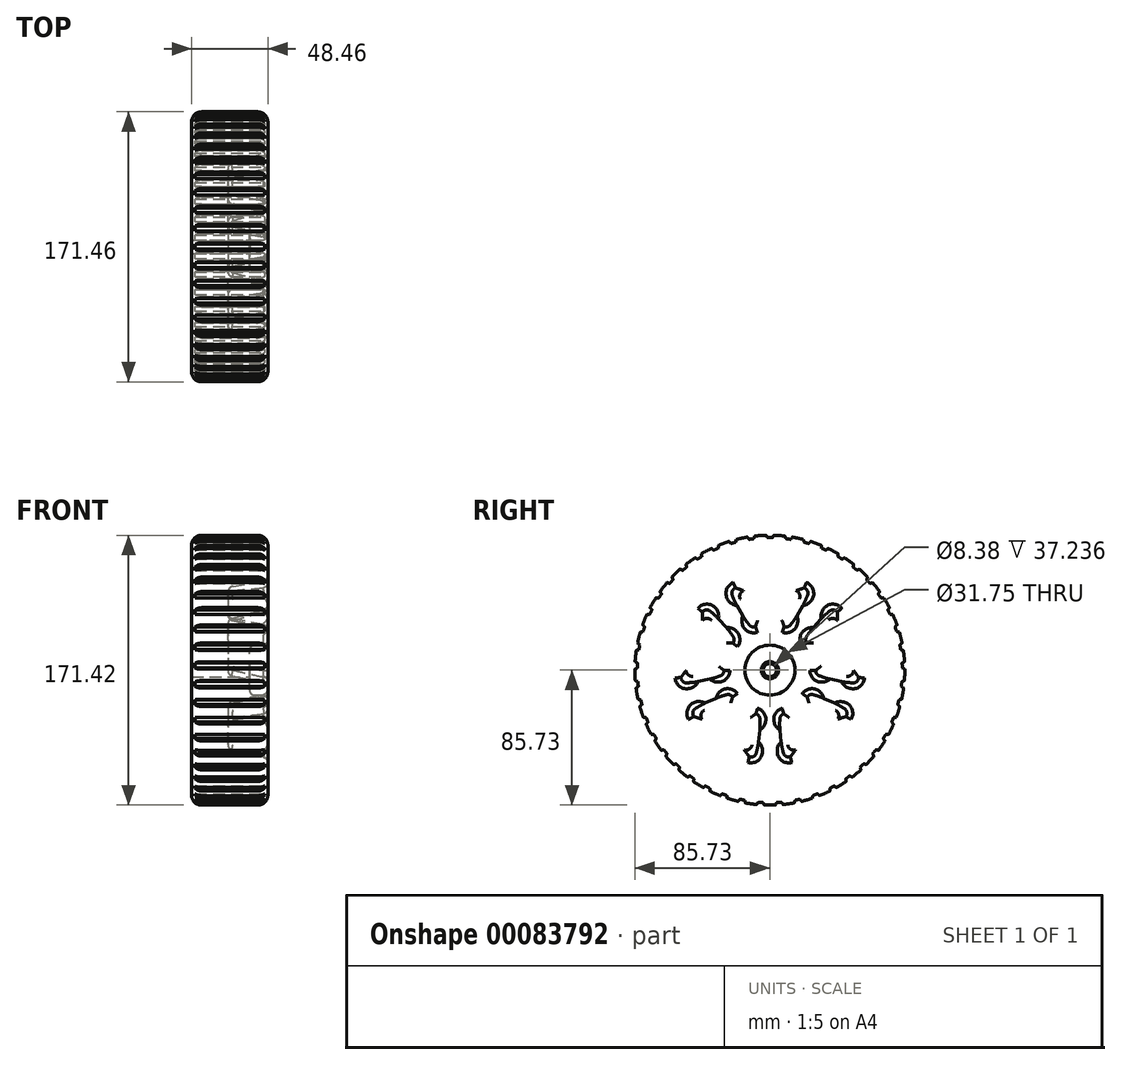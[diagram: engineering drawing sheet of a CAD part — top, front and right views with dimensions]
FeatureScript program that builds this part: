
annotation { "Feature Type Name" : "Feature", "Feature Type Description" : "" }
export const myFeature = defineFeature(function(context is Context, id is Id, definition is map)
    precondition{}
    {
        {
            var Q0;
            Q0=qCreatedBy(makeId("Front.planeOp"),FACE);
            var sketch = newSketch(context, id + "F0", { "sketchPlane" : qUnion([Q0])});
            skLineSegment(sketch, "E0", {"start": v(0, 85.73) * mm, "end": v(17.78, 85.73) * mm});
            skLineSegment(sketch, "E1", {"start": v(24.13, 79.38) * mm, "end": v(24.13, 19.05) * mm});
            skLineSegment(sketch, "E2", {"start": v(20.96, 15.88) * mm, "end": v(15.67, 15.88) * mm});
            skLineSegment(sketch, "E3", {"start": v(12.5, 12.7) * mm, "end": v(12.5, 5.46) * mm});
            skLineSegment(sketch, "E4", {"start": v(27.52, 0) * mm, "end": v(-27.22, 0) * mm});
            skLineSegment(sketch, "E5", {"start": v(0, 85.73) * mm, "end": v(-17.98, 85.73) * mm});
            skLineSegment(sketch, "E6", {"start": v(-24.33, 79.38) * mm, "end": v(-24.33, 4.2) * mm});
            skLineSegment(sketch, "E7", {"start": v(-24.33, 4.2) * mm, "end": v(12.9, 4.2) * mm});
            skPoint(sketch, "E8.end.orphan", {"position": v(0, 7.03) * mm});
            skLineSegment(sketch, "E9", {"start": v(12.5, 5.46) * mm, "end": v(12.9, 5.46) * mm});
            skLineSegment(sketch, "E10", {"start": v(12.9, 5.46) * mm, "end": v(12.9, 4.2) * mm});
            skPoint(sketch, "E11.visualSharp", {"position": v(-24.33, 85.73) * mm});
            skArc(sketch, "E11.filletArc", {"start": v(-17.98, 85.73) * mm, "mid": v(-22.47, 83.87) * mm, "end": v(-24.33, 79.38) * mm});
            skPoint(sketch, "E12.visualSharp", {"position": v(24.13, 85.73) * mm});
            skArc(sketch, "E12.filletArc", {"start": v(24.13, 79.38) * mm, "mid": v(22.27, 83.87) * mm, "end": v(17.78, 85.73) * mm});
            skPoint(sketch, "E13.visualSharp", {"position": v(24.13, 15.88) * mm});
            skArc(sketch, "E13.filletArc", {"start": v(20.96, 15.88) * mm, "mid": v(23.2, 16.8) * mm, "end": v(24.13, 19.05) * mm});
            skPoint(sketch, "E14.visualSharp", {"position": v(12.5, 15.88) * mm});
            skArc(sketch, "E14.filletArc", {"start": v(15.67, 15.88) * mm, "mid": v(13.43, 14.95) * mm, "end": v(12.5, 12.7) * mm});
            skSolve(sketch);
        }
        {
            var Q0;
            Q0=makeQuery(id+"F0.imprint","IMPRINT",FACE,{"disambiguationData":[TD([[makeQuery(id+"F0.imprint","IMPRINT",EDGE,{"derivedFrom":sQuery(id+"F0.wireOp",EDGE,"E0")}),-1.0]])]});
            var Q1;
            Q1=sQuery(id+"F0.wireOp",EDGE,"E4");
            revolve(context, id + "F1", {"entities" : qUnion([Q0]), "axis" : qUnion([Q1]), "revolveType" : RevolveType.FULL});
        }
        {
            var Q0;
            Q0=makeQuery(id+"F1.opRevolve","SWEPT_FACE",FACE,{"disambiguationData":[OSD([sQuery(id+"F0.wireOp",EDGE,"E1")])]});
            var sketch = newSketch(context, id + "F2", { "sketchPlane" : qUnion([Q0])});
            skArc(sketch, "E15", {"start": v(12.14, 25.87) * mm, "mid": v(0, 28.58) * mm, "end": v(-12.14, 25.87) * mm});
            skArc(sketch, "E16", {"start": v(26.46, 50.66) * mm, "mid": v(0, 57.15) * mm, "end": v(-26.46, 50.66) * mm});
            skLineSegment(sketch, "E17", {"start": v(-12.14, 25.87) * mm, "end": v(-26.46, 50.66) * mm});
            skLineSegment(sketch, "E18", {"start": v(12.14, 25.87) * mm, "end": v(26.46, 50.66) * mm});
            skPoint(sketch, "E19.visualSharp", {"position": v(-26.46, 50.66) * mm});
            skPoint(sketch, "E20.visualSharp", {"position": v(26.46, 50.66) * mm});
            skPoint(sketch, "E21.visualSharp", {"position": v(12.14, 25.87) * mm});
            skPoint(sketch, "E22.visualSharp", {"position": v(-12.14, 25.87) * mm});
            skLineSegment(sketch, "E23.1.0", {"start": v(-28.35, -3.56) * mm, "end": v(-56.35, -9.5) * mm});
            skArc(sketch, "E23.1.1", {"start": v(-40, 40.82) * mm, "mid": v(-54.35, 17.66) * mm, "end": v(-56.35, -9.5) * mm});
            skLineSegment(sketch, "E23.1.2", {"start": v(-20.85, 19.54) * mm, "end": v(-40, 40.82) * mm});
            skArc(sketch, "E23.1.3", {"start": v(-20.85, 19.54) * mm, "mid": v(-27.18, 8.83) * mm, "end": v(-28.35, -3.56) * mm});
            skLineSegment(sketch, "E23.2.0", {"start": v(-5.38, -28.06) * mm, "end": v(-8.37, -56.53) * mm});
            skArc(sketch, "E23.2.1", {"start": v(-51.18, -25.43) * mm, "mid": v(-33.6, -46.24) * mm, "end": v(-8.37, -56.53) * mm});
            skLineSegment(sketch, "E23.2.2", {"start": v(-25.03, -13.79) * mm, "end": v(-51.18, -25.43) * mm});
            skArc(sketch, "E23.2.3", {"start": v(-25.03, -13.79) * mm, "mid": v(-16.8, -23.12) * mm, "end": v(-5.38, -28.06) * mm});
            skLineSegment(sketch, "E23.3.0", {"start": v(25.03, -13.79) * mm, "end": v(51.18, -25.43) * mm});
            skArc(sketch, "E23.3.1", {"start": v(8.37, -56.53) * mm, "mid": v(33.6, -46.24) * mm, "end": v(51.18, -25.43) * mm});
            skLineSegment(sketch, "E23.3.2", {"start": v(5.38, -28.06) * mm, "end": v(8.37, -56.53) * mm});
            skArc(sketch, "E23.3.3", {"start": v(5.38, -28.06) * mm, "mid": v(16.8, -23.12) * mm, "end": v(25.03, -13.79) * mm});
            skLineSegment(sketch, "E23.4.0", {"start": v(20.85, 19.54) * mm, "end": v(40, 40.82) * mm});
            skArc(sketch, "E23.4.1", {"start": v(56.35, -9.5) * mm, "mid": v(54.35, 17.66) * mm, "end": v(40, 40.82) * mm});
            skLineSegment(sketch, "E23.4.2", {"start": v(28.35, -3.56) * mm, "end": v(56.35, -9.5) * mm});
            skArc(sketch, "E23.4.3", {"start": v(28.35, -3.56) * mm, "mid": v(27.18, 8.83) * mm, "end": v(20.85, 19.54) * mm});
            skSolve(sketch);
        }
        {
            var Q0;
            Q0 = qSketchRegion(id + "F2", true);
            extrude(context, id + "F3", {"entities" : qUnion([Q0]), "operationType" : NewBodyOperationType.REMOVE, "oppositeDirection" : true, "depth" : 25.4 * mm, "hasDraft" : true, "draftAngle" : 10 * degree, "draftPullDirection" : true});
        }
        {
            var Q0;
            Q0=makeQuery(id+"F3.boolean.opBoolean","COPY",FACE,{"derivedFrom":makeQuery(id+"F3.opExtrude","SWEPT_FACE",FACE,{"disambiguationData":[OSD([sQuery(id+"F2.wireOp",EDGE,"E16")])]})});
            var Q1;
            Q1=makeQuery(id+"F3.boolean.opBoolean","COPY",FACE,{"derivedFrom":makeQuery(id+"F3.opExtrude","SWEPT_FACE",FACE,{"disambiguationData":[OSD([sQuery(id+"F2.wireOp",EDGE,"E15")])]})});
            var Q2;
            Q2=makeQuery(id+"F3.boolean.opBoolean","COPY",FACE,{"derivedFrom":makeQuery(id+"F3.opExtrude","CAP_FACE",FACE,{"disambiguationData":[OSD([sQuery(id+"F2.wireOp",EDGE,"E15"),sQuery(id+"F2.wireOp",EDGE,"E16"),sQuery(id+"F2.wireOp",EDGE,"E17"),sQuery(id+"F2.wireOp",EDGE,"E18")])],"isStart":false})});
            var Q3;
            Q3=makeQuery(id+"F3.boolean.opBoolean","COPY",FACE,{"derivedFrom":makeQuery(id+"F3.opExtrude","CAP_FACE",FACE,{"disambiguationData":[OSD([sQuery(id+"F2.wireOp",EDGE,"E23.1.0"),sQuery(id+"F2.wireOp",EDGE,"E23.1.1"),sQuery(id+"F2.wireOp",EDGE,"E23.1.2"),sQuery(id+"F2.wireOp",EDGE,"E23.1.3")])],"isStart":false})});
            var Q4;
            Q4=makeQuery(id+"F3.boolean.opBoolean","COPY",FACE,{"derivedFrom":makeQuery(id+"F3.opExtrude","SWEPT_FACE",FACE,{"disambiguationData":[OSD([sQuery(id+"F2.wireOp",EDGE,"E23.1.1")])]})});
            var Q5;
            Q5=makeQuery(id+"F3.boolean.opBoolean","COPY",FACE,{"derivedFrom":makeQuery(id+"F3.opExtrude","SWEPT_FACE",FACE,{"disambiguationData":[OSD([sQuery(id+"F2.wireOp",EDGE,"E23.1.3")])]})});
            var Q6;
            Q6=makeQuery(id+"F3.boolean.opBoolean","COPY",FACE,{"derivedFrom":makeQuery(id+"F3.opExtrude","CAP_FACE",FACE,{"disambiguationData":[OSD([sQuery(id+"F2.wireOp",EDGE,"E23.3.0"),sQuery(id+"F2.wireOp",EDGE,"E23.3.1"),sQuery(id+"F2.wireOp",EDGE,"E23.3.2"),sQuery(id+"F2.wireOp",EDGE,"E23.3.3")])],"isStart":false})});
            var Q7;
            Q7=makeQuery(id+"F3.boolean.opBoolean","COPY",FACE,{"derivedFrom":makeQuery(id+"F3.opExtrude","CAP_FACE",FACE,{"disambiguationData":[OSD([sQuery(id+"F2.wireOp",EDGE,"E23.2.0"),sQuery(id+"F2.wireOp",EDGE,"E23.2.1"),sQuery(id+"F2.wireOp",EDGE,"E23.2.2"),sQuery(id+"F2.wireOp",EDGE,"E23.2.3")])],"isStart":false})});
            var Q8;
            Q8=makeQuery(id+"F3.boolean.opBoolean","COPY",FACE,{"derivedFrom":makeQuery(id+"F3.opExtrude","SWEPT_FACE",FACE,{"disambiguationData":[OSD([sQuery(id+"F2.wireOp",EDGE,"E23.2.3")])]})});
            var Q9;
            Q9=makeQuery(id+"F3.boolean.opBoolean","COPY",FACE,{"derivedFrom":makeQuery(id+"F3.opExtrude","SWEPT_FACE",FACE,{"disambiguationData":[OSD([sQuery(id+"F2.wireOp",EDGE,"E23.3.3")])]})});
            var Q10;
            Q10=makeQuery(id+"F3.boolean.opBoolean","COPY",FACE,{"derivedFrom":makeQuery(id+"F3.opExtrude","SWEPT_FACE",FACE,{"disambiguationData":[OSD([sQuery(id+"F2.wireOp",EDGE,"E23.4.3")])]})});
            var Q11;
            Q11=makeQuery(id+"F3.boolean.opBoolean","COPY",FACE,{"derivedFrom":makeQuery(id+"F3.opExtrude","CAP_FACE",FACE,{"disambiguationData":[OSD([sQuery(id+"F2.wireOp",EDGE,"E23.4.0"),sQuery(id+"F2.wireOp",EDGE,"E23.4.1"),sQuery(id+"F2.wireOp",EDGE,"E23.4.2"),sQuery(id+"F2.wireOp",EDGE,"E23.4.3")])],"isStart":false})});
            var Q12;
            Q12=makeQuery(id+"F3.boolean.opBoolean","COPY",FACE,{"derivedFrom":makeQuery(id+"F3.opExtrude","SWEPT_FACE",FACE,{"disambiguationData":[OSD([sQuery(id+"F2.wireOp",EDGE,"E23.4.1")])]})});
            var Q13;
            Q13=makeQuery(id+"F3.boolean.opBoolean","COPY",FACE,{"derivedFrom":makeQuery(id+"F3.opExtrude","SWEPT_FACE",FACE,{"disambiguationData":[OSD([sQuery(id+"F2.wireOp",EDGE,"E23.3.1")])]})});
            var Q14;
            Q14=makeQuery(id+"F3.boolean.opBoolean","COPY",FACE,{"derivedFrom":makeQuery(id+"F3.opExtrude","SWEPT_FACE",FACE,{"disambiguationData":[OSD([sQuery(id+"F2.wireOp",EDGE,"E23.2.1")])]})});
            fillet(context, id + "F4", {"entities" : qUnion([Q0, Q1, Q2, Q3, Q4, Q5, Q6, Q7, Q8, Q9, Q10, Q11, Q12, Q13, Q14]), "radius" : 3.8 * mm, "tangentPropagation" : true, "allowEdgeOverflow" : false});
        }
        {
            var Q0;
            Q0=qCreatedBy(makeId("Right.planeOp"),FACE);
            var sketch = newSketch(context, id + "F5", { "sketchPlane" : qUnion([Q0])});
            skLineSegment(sketch, "E24", {"start": v(-1.59, 84.14) * mm, "end": v(1.59, 84.14) * mm});
            skLineSegment(sketch, "E25", {"start": v(-1.59, 84.14) * mm, "end": v(-3.18, 87.34) * mm});
            skLineSegment(sketch, "E26", {"start": v(1.59, 84.14) * mm, "end": v(3.17, 87.34) * mm});
            skLineSegment(sketch, "E27", {"start": v(-3.18, 87.34) * mm, "end": v(3.18, 87.34) * mm});
            skLineSegment(sketch, "E28.1.0", {"start": v(-15.3, 86.05) * mm, "end": v(-9.01, 86.94) * mm});
            skLineSegment(sketch, "E28.1.1", {"start": v(-13.28, 83.1) * mm, "end": v(-10.14, 83.54) * mm});
            skLineSegment(sketch, "E28.1.2", {"start": v(-10.14, 83.54) * mm, "end": v(-9.01, 86.94) * mm});
            skLineSegment(sketch, "E28.1.3", {"start": v(-13.28, 83.1) * mm, "end": v(-15.3, 86.05) * mm});
            skLineSegment(sketch, "E28.2.0", {"start": v(-27.13, 83.09) * mm, "end": v(-21.02, 84.84) * mm});
            skLineSegment(sketch, "E28.2.1", {"start": v(-24.72, 80.44) * mm, "end": v(-21.67, 81.32) * mm});
            skLineSegment(sketch, "E28.2.2", {"start": v(-21.67, 81.32) * mm, "end": v(-21.02, 84.84) * mm});
            skLineSegment(sketch, "E28.2.3", {"start": v(-24.72, 80.44) * mm, "end": v(-27.13, 83.09) * mm});
            skLineSegment(sketch, "E28.3.0", {"start": v(-38.43, 78.5) * mm, "end": v(-32.63, 81.08) * mm});
            skLineSegment(sketch, "E28.3.1", {"start": v(-35.67, 76.22) * mm, "end": v(-32.77, 77.5) * mm});
            skLineSegment(sketch, "E28.3.2", {"start": v(-32.77, 77.5) * mm, "end": v(-32.63, 81.08) * mm});
            skLineSegment(sketch, "E28.3.3", {"start": v(-35.67, 76.22) * mm, "end": v(-38.43, 78.5) * mm});
            skLineSegment(sketch, "E28.4.0", {"start": v(-48.98, 72.4) * mm, "end": v(-43.6, 75.76) * mm});
            skLineSegment(sketch, "E28.4.1", {"start": v(-45.93, 70.51) * mm, "end": v(-43.24, 72.2) * mm});
            skLineSegment(sketch, "E28.4.2", {"start": v(-43.24, 72.2) * mm, "end": v(-43.6, 75.76) * mm});
            skLineSegment(sketch, "E28.4.3", {"start": v(-45.93, 70.51) * mm, "end": v(-48.98, 72.4) * mm});
            skLineSegment(sketch, "E28.5.0", {"start": v(-58.58, 64.87) * mm, "end": v(-53.71, 68.95) * mm});
            skLineSegment(sketch, "E28.5.1", {"start": v(-55.3, 63.43) * mm, "end": v(-52.87, 65.47) * mm});
            skLineSegment(sketch, "E28.5.2", {"start": v(-52.87, 65.47) * mm, "end": v(-53.71, 68.95) * mm});
            skLineSegment(sketch, "E28.5.3", {"start": v(-55.3, 63.43) * mm, "end": v(-58.58, 64.87) * mm});
            skLineSegment(sketch, "E28.6.0", {"start": v(-67.03, 56.09) * mm, "end": v(-62.79, 60.8) * mm});
            skLineSegment(sketch, "E28.6.1", {"start": v(-63.59, 55.12) * mm, "end": v(-61.46, 57.48) * mm});
            skLineSegment(sketch, "E28.6.2", {"start": v(-61.46, 57.48) * mm, "end": v(-62.79, 60.8) * mm});
            skLineSegment(sketch, "E28.6.3", {"start": v(-63.59, 55.12) * mm, "end": v(-67.03, 56.09) * mm});
            skLineSegment(sketch, "E28.7.0", {"start": v(-74.19, 46.21) * mm, "end": v(-70.64, 51.47) * mm});
            skLineSegment(sketch, "E28.7.1", {"start": v(-70.64, 45.73) * mm, "end": v(-68.87, 48.37) * mm});
            skLineSegment(sketch, "E28.7.2", {"start": v(-68.87, 48.37) * mm, "end": v(-70.64, 51.47) * mm});
            skLineSegment(sketch, "E28.7.3", {"start": v(-70.64, 45.73) * mm, "end": v(-74.19, 46.21) * mm});
            skLineSegment(sketch, "E28.8.0", {"start": v(-79.9, 35.44) * mm, "end": v(-77.11, 41.14) * mm});
            skLineSegment(sketch, "E28.8.1", {"start": v(-76.32, 35.46) * mm, "end": v(-74.93, 38.31) * mm});
            skLineSegment(sketch, "E28.8.2", {"start": v(-74.93, 38.31) * mm, "end": v(-77.11, 41.14) * mm});
            skLineSegment(sketch, "E28.8.3", {"start": v(-76.32, 35.46) * mm, "end": v(-79.9, 35.44) * mm});
            skLineSegment(sketch, "E28.9.0", {"start": v(-84.05, 23.97) * mm, "end": v(-82.09, 30.01) * mm});
            skLineSegment(sketch, "E28.9.1", {"start": v(-80.51, 24.5) * mm, "end": v(-79.53, 27.5) * mm});
            skLineSegment(sketch, "E28.9.2", {"start": v(-79.53, 27.5) * mm, "end": v(-82.09, 30.01) * mm});
            skLineSegment(sketch, "E28.9.3", {"start": v(-80.51, 24.5) * mm, "end": v(-84.05, 23.97) * mm});
            skLineSegment(sketch, "E28.10.0", {"start": v(-86.57, 12.04) * mm, "end": v(-85.47, 18.3) * mm});
            skLineSegment(sketch, "E28.10.1", {"start": v(-83.13, 13.05) * mm, "end": v(-82.58, 16.17) * mm});
            skLineSegment(sketch, "E28.10.2", {"start": v(-82.58, 16.17) * mm, "end": v(-85.47, 18.3) * mm});
            skLineSegment(sketch, "E28.10.3", {"start": v(-83.13, 13.05) * mm, "end": v(-86.57, 12.04) * mm});
            skLineSegment(sketch, "E28.11.0", {"start": v(-87.4, -0.12) * mm, "end": v(-87.18, 6.22) * mm});
            skLineSegment(sketch, "E28.11.1", {"start": v(-84.14, 1.35) * mm, "end": v(-84.03, 4.52) * mm});
            skLineSegment(sketch, "E28.11.2", {"start": v(-84.03, 4.52) * mm, "end": v(-87.18, 6.22) * mm});
            skLineSegment(sketch, "E28.11.3", {"start": v(-84.14, 1.35) * mm, "end": v(-87.4, -0.12) * mm});
            skLineSegment(sketch, "E28.12.0", {"start": v(-86.53, -12.29) * mm, "end": v(-87.2, -5.97) * mm});
            skLineSegment(sketch, "E28.12.1", {"start": v(-83.51, -10.37) * mm, "end": v(-83.84, -7.22) * mm});
            skLineSegment(sketch, "E28.12.2", {"start": v(-83.84, -7.22) * mm, "end": v(-87.2, -5.97) * mm});
            skLineSegment(sketch, "E28.12.3", {"start": v(-83.51, -10.37) * mm, "end": v(-86.53, -12.29) * mm});
            skLineSegment(sketch, "E28.13.0", {"start": v(-83.98, -24.21) * mm, "end": v(-85.52, -18.05) * mm});
            skLineSegment(sketch, "E28.13.1", {"start": v(-81.25, -21.9) * mm, "end": v(-82.02, -18.81) * mm});
            skLineSegment(sketch, "E28.13.2", {"start": v(-82.02, -18.81) * mm, "end": v(-85.52, -18.05) * mm});
            skLineSegment(sketch, "E28.13.3", {"start": v(-81.25, -21.9) * mm, "end": v(-83.98, -24.21) * mm});
            skLineSegment(sketch, "E28.14.0", {"start": v(-79.8, -35.66) * mm, "end": v(-82.17, -29.78) * mm});
            skLineSegment(sketch, "E28.14.1", {"start": v(-77.42, -33) * mm, "end": v(-78.6, -30.05) * mm});
            skLineSegment(sketch, "E28.14.2", {"start": v(-78.6, -30.05) * mm, "end": v(-82.17, -29.78) * mm});
            skLineSegment(sketch, "E28.14.3", {"start": v(-77.42, -33) * mm, "end": v(-79.8, -35.66) * mm});
            skLineSegment(sketch, "E28.15.0", {"start": v(-74.06, -46.42) * mm, "end": v(-77.23, -40.92) * mm});
            skLineSegment(sketch, "E28.15.1", {"start": v(-72.07, -43.44) * mm, "end": v(-73.66, -40.7) * mm});
            skLineSegment(sketch, "E28.15.2", {"start": v(-73.66, -40.7) * mm, "end": v(-77.23, -40.92) * mm});
            skLineSegment(sketch, "E28.15.3", {"start": v(-72.07, -43.44) * mm, "end": v(-74.06, -46.42) * mm});
            skLineSegment(sketch, "E28.16.0", {"start": v(-66.87, -56.28) * mm, "end": v(-70.78, -51.27) * mm});
            skLineSegment(sketch, "E28.16.1", {"start": v(-65.32, -53.05) * mm, "end": v(-67.28, -50.55) * mm});
            skLineSegment(sketch, "E28.16.2", {"start": v(-67.28, -50.55) * mm, "end": v(-70.78, -51.27) * mm});
            skLineSegment(sketch, "E28.16.3", {"start": v(-65.32, -53.05) * mm, "end": v(-66.87, -56.28) * mm});
            skLineSegment(sketch, "E28.17.0", {"start": v(-58.4, -65.04) * mm, "end": v(-62.96, -60.63) * mm});
            skLineSegment(sketch, "E28.17.1", {"start": v(-57.3, -61.63) * mm, "end": v(-59.59, -59.42) * mm});
            skLineSegment(sketch, "E28.17.2", {"start": v(-59.59, -59.42) * mm, "end": v(-62.96, -60.63) * mm});
            skLineSegment(sketch, "E28.17.3", {"start": v(-57.3, -61.63) * mm, "end": v(-58.4, -65.04) * mm});
            skLineSegment(sketch, "E28.18.0", {"start": v(-48.77, -72.53) * mm, "end": v(-53.9, -68.8) * mm});
            skLineSegment(sketch, "E28.18.1", {"start": v(-48.17, -69) * mm, "end": v(-50.74, -67.14) * mm});
            skLineSegment(sketch, "E28.18.2", {"start": v(-50.74, -67.14) * mm, "end": v(-53.9, -68.8) * mm});
            skLineSegment(sketch, "E28.18.3", {"start": v(-48.17, -69) * mm, "end": v(-48.77, -72.53) * mm});
            skLineSegment(sketch, "E28.19.0", {"start": v(-38.2, -78.61) * mm, "end": v(-43.8, -75.63) * mm});
            skLineSegment(sketch, "E28.19.1", {"start": v(-38.1, -75.03) * mm, "end": v(-40.9, -73.54) * mm});
            skLineSegment(sketch, "E28.19.2", {"start": v(-40.9, -73.54) * mm, "end": v(-43.8, -75.63) * mm});
            skLineSegment(sketch, "E28.19.3", {"start": v(-38.1, -75.03) * mm, "end": v(-38.2, -78.61) * mm});
            skLineSegment(sketch, "E28.20.0", {"start": v(-26.9, -83.16) * mm, "end": v(-32.86, -81) * mm});
            skLineSegment(sketch, "E28.20.1", {"start": v(-27.28, -79.6) * mm, "end": v(-30.27, -78.52) * mm});
            skLineSegment(sketch, "E28.20.2", {"start": v(-30.27, -78.52) * mm, "end": v(-32.86, -81) * mm});
            skLineSegment(sketch, "E28.20.3", {"start": v(-27.28, -79.6) * mm, "end": v(-26.9, -83.16) * mm});
            skLineSegment(sketch, "E28.21.0", {"start": v(-15.05, -86.1) * mm, "end": v(-21.27, -84.78) * mm});
            skLineSegment(sketch, "E28.21.1", {"start": v(-15.94, -82.63) * mm, "end": v(-19.05, -81.97) * mm});
            skLineSegment(sketch, "E28.21.2", {"start": v(-19.05, -81.97) * mm, "end": v(-21.27, -84.78) * mm});
            skLineSegment(sketch, "E28.21.3", {"start": v(-15.94, -82.63) * mm, "end": v(-15.05, -86.1) * mm});
            skLineSegment(sketch, "E28.22.0", {"start": v(-2.93, -87.35) * mm, "end": v(-9.26, -86.91) * mm});
            skLineSegment(sketch, "E28.22.1", {"start": v(-4.29, -84.04) * mm, "end": v(-7.45, -83.82) * mm});
            skLineSegment(sketch, "E28.22.2", {"start": v(-7.45, -83.82) * mm, "end": v(-9.26, -86.91) * mm});
            skLineSegment(sketch, "E28.22.3", {"start": v(-4.29, -84.04) * mm, "end": v(-2.93, -87.35) * mm});
            skLineSegment(sketch, "E28.23.0", {"start": v(9.26, -86.91) * mm, "end": v(2.93, -87.35) * mm});
            skLineSegment(sketch, "E28.23.1", {"start": v(7.45, -83.82) * mm, "end": v(4.29, -84.04) * mm});
            skLineSegment(sketch, "E28.23.2", {"start": v(4.29, -84.04) * mm, "end": v(2.93, -87.35) * mm});
            skLineSegment(sketch, "E28.23.3", {"start": v(7.45, -83.82) * mm, "end": v(9.26, -86.91) * mm});
            skLineSegment(sketch, "E28.24.0", {"start": v(21.27, -84.78) * mm, "end": v(15.05, -86.1) * mm});
            skLineSegment(sketch, "E28.24.1", {"start": v(19.05, -81.97) * mm, "end": v(15.94, -82.63) * mm});
            skLineSegment(sketch, "E28.24.2", {"start": v(15.94, -82.63) * mm, "end": v(15.05, -86.1) * mm});
            skLineSegment(sketch, "E28.24.3", {"start": v(19.05, -81.97) * mm, "end": v(21.27, -84.78) * mm});
            skPoint(sketch, "E28.center", {"position": v(0, 0) * mm});
            skLineSegment(sketch, "E29.1.25.0", {"start": v(32.86, -81) * mm, "end": v(26.9, -83.16) * mm});
            skLineSegment(sketch, "E29.3.25.0", {"start": v(30.27, -78.52) * mm, "end": v(27.28, -79.6) * mm});
            skLineSegment(sketch, "E29.6.25.0", {"start": v(27.28, -79.6) * mm, "end": v(26.9, -83.16) * mm});
            skLineSegment(sketch, "E29.9.25.0", {"start": v(30.27, -78.52) * mm, "end": v(32.86, -81) * mm});
            skLineSegment(sketch, "E29.1.26.0", {"start": v(43.8, -75.63) * mm, "end": v(38.2, -78.61) * mm});
            skLineSegment(sketch, "E29.3.26.0", {"start": v(40.9, -73.54) * mm, "end": v(38.1, -75.03) * mm});
            skLineSegment(sketch, "E29.6.26.0", {"start": v(38.1, -75.03) * mm, "end": v(38.2, -78.61) * mm});
            skLineSegment(sketch, "E29.9.26.0", {"start": v(40.9, -73.54) * mm, "end": v(43.8, -75.63) * mm});
            skLineSegment(sketch, "E29.1.27.0", {"start": v(53.9, -68.8) * mm, "end": v(48.77, -72.53) * mm});
            skLineSegment(sketch, "E29.3.27.0", {"start": v(50.74, -67.14) * mm, "end": v(48.17, -69) * mm});
            skLineSegment(sketch, "E29.6.27.0", {"start": v(48.17, -69) * mm, "end": v(48.77, -72.53) * mm});
            skLineSegment(sketch, "E29.9.27.0", {"start": v(50.74, -67.14) * mm, "end": v(53.9, -68.8) * mm});
            skLineSegment(sketch, "E29.1.28.0", {"start": v(62.96, -60.63) * mm, "end": v(58.4, -65.04) * mm});
            skLineSegment(sketch, "E29.3.28.0", {"start": v(59.59, -59.42) * mm, "end": v(57.3, -61.63) * mm});
            skLineSegment(sketch, "E29.6.28.0", {"start": v(57.3, -61.63) * mm, "end": v(58.4, -65.04) * mm});
            skLineSegment(sketch, "E29.9.28.0", {"start": v(59.59, -59.42) * mm, "end": v(62.96, -60.63) * mm});
            skLineSegment(sketch, "E29.1.29.0", {"start": v(70.78, -51.27) * mm, "end": v(66.87, -56.28) * mm});
            skLineSegment(sketch, "E29.3.29.0", {"start": v(67.28, -50.55) * mm, "end": v(65.32, -53.05) * mm});
            skLineSegment(sketch, "E29.6.29.0", {"start": v(65.32, -53.05) * mm, "end": v(66.87, -56.28) * mm});
            skLineSegment(sketch, "E29.9.29.0", {"start": v(67.28, -50.55) * mm, "end": v(70.78, -51.27) * mm});
            skLineSegment(sketch, "E29.1.30.0", {"start": v(77.23, -40.92) * mm, "end": v(74.06, -46.42) * mm});
            skLineSegment(sketch, "E29.3.30.0", {"start": v(73.66, -40.7) * mm, "end": v(72.07, -43.44) * mm});
            skLineSegment(sketch, "E29.6.30.0", {"start": v(72.07, -43.44) * mm, "end": v(74.06, -46.42) * mm});
            skLineSegment(sketch, "E29.9.30.0", {"start": v(73.66, -40.7) * mm, "end": v(77.23, -40.92) * mm});
            skLineSegment(sketch, "E29.1.31.0", {"start": v(82.17, -29.78) * mm, "end": v(79.8, -35.66) * mm});
            skLineSegment(sketch, "E29.3.31.0", {"start": v(78.6, -30.05) * mm, "end": v(77.42, -33) * mm});
            skLineSegment(sketch, "E29.6.31.0", {"start": v(77.42, -33) * mm, "end": v(79.8, -35.66) * mm});
            skLineSegment(sketch, "E29.9.31.0", {"start": v(78.6, -30.05) * mm, "end": v(82.17, -29.78) * mm});
            skLineSegment(sketch, "E29.1.32.0", {"start": v(85.52, -18.05) * mm, "end": v(83.98, -24.21) * mm});
            skLineSegment(sketch, "E29.3.32.0", {"start": v(82.02, -18.81) * mm, "end": v(81.25, -21.9) * mm});
            skLineSegment(sketch, "E29.6.32.0", {"start": v(81.25, -21.9) * mm, "end": v(83.98, -24.21) * mm});
            skLineSegment(sketch, "E29.9.32.0", {"start": v(82.02, -18.81) * mm, "end": v(85.52, -18.05) * mm});
            skLineSegment(sketch, "E29.1.33.0", {"start": v(87.2, -5.97) * mm, "end": v(86.53, -12.29) * mm});
            skLineSegment(sketch, "E29.3.33.0", {"start": v(83.84, -7.22) * mm, "end": v(83.51, -10.37) * mm});
            skLineSegment(sketch, "E29.6.33.0", {"start": v(83.51, -10.37) * mm, "end": v(86.53, -12.29) * mm});
            skLineSegment(sketch, "E29.9.33.0", {"start": v(83.84, -7.22) * mm, "end": v(87.2, -5.97) * mm});
            skLineSegment(sketch, "E29.1.34.0", {"start": v(87.18, 6.22) * mm, "end": v(87.4, -0.12) * mm});
            skLineSegment(sketch, "E29.3.34.0", {"start": v(84.03, 4.52) * mm, "end": v(84.14, 1.35) * mm});
            skLineSegment(sketch, "E29.6.34.0", {"start": v(84.14, 1.35) * mm, "end": v(87.4, -0.12) * mm});
            skLineSegment(sketch, "E29.9.34.0", {"start": v(84.03, 4.52) * mm, "end": v(87.18, 6.22) * mm});
            skLineSegment(sketch, "E30.1.35.0", {"start": v(85.47, 18.3) * mm, "end": v(86.57, 12.04) * mm});
            skLineSegment(sketch, "E30.3.35.0", {"start": v(82.58, 16.17) * mm, "end": v(83.13, 13.05) * mm});
            skLineSegment(sketch, "E30.6.35.0", {"start": v(83.13, 13.05) * mm, "end": v(86.57, 12.04) * mm});
            skLineSegment(sketch, "E30.9.35.0", {"start": v(82.58, 16.17) * mm, "end": v(85.47, 18.3) * mm});
            skLineSegment(sketch, "E30.1.36.0", {"start": v(82.09, 30.01) * mm, "end": v(84.05, 23.97) * mm});
            skLineSegment(sketch, "E30.3.36.0", {"start": v(79.53, 27.5) * mm, "end": v(80.51, 24.5) * mm});
            skLineSegment(sketch, "E30.6.36.0", {"start": v(80.51, 24.5) * mm, "end": v(84.05, 23.97) * mm});
            skLineSegment(sketch, "E30.9.36.0", {"start": v(79.53, 27.5) * mm, "end": v(82.09, 30.01) * mm});
            skLineSegment(sketch, "E30.1.37.0", {"start": v(77.11, 41.14) * mm, "end": v(79.9, 35.44) * mm});
            skLineSegment(sketch, "E30.3.37.0", {"start": v(74.93, 38.31) * mm, "end": v(76.32, 35.46) * mm});
            skLineSegment(sketch, "E30.6.37.0", {"start": v(76.32, 35.46) * mm, "end": v(79.9, 35.44) * mm});
            skLineSegment(sketch, "E30.9.37.0", {"start": v(74.93, 38.31) * mm, "end": v(77.11, 41.14) * mm});
            skLineSegment(sketch, "E30.1.38.0", {"start": v(70.64, 51.47) * mm, "end": v(74.19, 46.21) * mm});
            skLineSegment(sketch, "E30.3.38.0", {"start": v(68.87, 48.37) * mm, "end": v(70.64, 45.73) * mm});
            skLineSegment(sketch, "E30.6.38.0", {"start": v(70.64, 45.73) * mm, "end": v(74.19, 46.21) * mm});
            skLineSegment(sketch, "E30.9.38.0", {"start": v(68.87, 48.37) * mm, "end": v(70.64, 51.47) * mm});
            skLineSegment(sketch, "E30.1.39.0", {"start": v(62.79, 60.8) * mm, "end": v(67.03, 56.09) * mm});
            skLineSegment(sketch, "E30.3.39.0", {"start": v(61.46, 57.48) * mm, "end": v(63.59, 55.12) * mm});
            skLineSegment(sketch, "E30.6.39.0", {"start": v(63.59, 55.12) * mm, "end": v(67.03, 56.09) * mm});
            skLineSegment(sketch, "E30.9.39.0", {"start": v(61.46, 57.48) * mm, "end": v(62.79, 60.8) * mm});
            skLineSegment(sketch, "E31.1.40.0", {"start": v(53.71, 68.95) * mm, "end": v(58.58, 64.87) * mm});
            skLineSegment(sketch, "E31.3.40.0", {"start": v(52.87, 65.47) * mm, "end": v(55.3, 63.43) * mm});
            skLineSegment(sketch, "E31.6.40.0", {"start": v(55.3, 63.43) * mm, "end": v(58.58, 64.87) * mm});
            skLineSegment(sketch, "E31.9.40.0", {"start": v(52.87, 65.47) * mm, "end": v(53.71, 68.95) * mm});
            skLineSegment(sketch, "E31.1.41.0", {"start": v(43.6, 75.76) * mm, "end": v(48.98, 72.4) * mm});
            skLineSegment(sketch, "E31.3.41.0", {"start": v(43.24, 72.2) * mm, "end": v(45.93, 70.51) * mm});
            skLineSegment(sketch, "E31.6.41.0", {"start": v(45.93, 70.51) * mm, "end": v(48.98, 72.4) * mm});
            skLineSegment(sketch, "E31.9.41.0", {"start": v(43.24, 72.2) * mm, "end": v(43.6, 75.76) * mm});
            skLineSegment(sketch, "E31.1.42.0", {"start": v(32.63, 81.08) * mm, "end": v(38.43, 78.5) * mm});
            skLineSegment(sketch, "E31.3.42.0", {"start": v(32.77, 77.5) * mm, "end": v(35.67, 76.22) * mm});
            skLineSegment(sketch, "E31.6.42.0", {"start": v(35.67, 76.22) * mm, "end": v(38.43, 78.5) * mm});
            skLineSegment(sketch, "E31.9.42.0", {"start": v(32.77, 77.5) * mm, "end": v(32.63, 81.08) * mm});
            skLineSegment(sketch, "E31.1.43.0", {"start": v(21.02, 84.84) * mm, "end": v(27.13, 83.09) * mm});
            skLineSegment(sketch, "E31.3.43.0", {"start": v(21.67, 81.32) * mm, "end": v(24.72, 80.44) * mm});
            skLineSegment(sketch, "E31.6.43.0", {"start": v(24.72, 80.44) * mm, "end": v(27.13, 83.09) * mm});
            skLineSegment(sketch, "E31.9.43.0", {"start": v(21.67, 81.32) * mm, "end": v(21.02, 84.84) * mm});
            skLineSegment(sketch, "E31.1.44.0", {"start": v(9.01, 86.94) * mm, "end": v(15.3, 86.05) * mm});
            skLineSegment(sketch, "E31.3.44.0", {"start": v(10.14, 83.54) * mm, "end": v(13.28, 83.1) * mm});
            skLineSegment(sketch, "E31.6.44.0", {"start": v(13.28, 83.1) * mm, "end": v(15.3, 86.05) * mm});
            skLineSegment(sketch, "E31.9.44.0", {"start": v(10.14, 83.54) * mm, "end": v(9.01, 86.94) * mm});
            skSolve(sketch);
        }
        {
            var Q0;
            Q0 = qSketchRegion(id + "F5", true);
            extrude(context, id + "F6", {"entities" : qUnion([Q0]), "operationType" : NewBodyOperationType.REMOVE, "oppositeDirection" : true, "depth" : 50.8 * mm, "symmetric" : true});
        }
        {
            var Q0;
            Q0=makeQuery(id+"F1.opRevolve","SWEPT_FACE",FACE,{"disambiguationData":[OSD([sQuery(id+"F0.wireOp",EDGE,"E1")])]});
            var sketch = newSketch(context, id + "F7", { "sketchPlane" : qUnion([Q0])});
            skSolve(sketch);
        }
        {
            var Q0;
            {var subQ0=sQuery(id+"F0.wireOp",EDGE,"E1");Q0=makeQuery(id+"F7.imprint","IMPRINT",FACE,{"disambiguationData":[TD([[makeQuery(id+"F7.imprint","IMPRINT",EDGE,{"derivedFrom":makeQuery(id+"F1.opRevolve","SWEPT_EDGE",EDGE,{"disambiguationData":[OSD([subQ0,sQuery(id+"F0.wireOp",EDGE,"E12.filletArc")])]})}),1.0]])]});}
            var sketch = newSketch(context, id + "F8", { "sketchPlane" : qUnion([Q0])});
            skCircle(sketch, "E32", {"center": v(0, 70.28) * mm, "radius": 5.5 * mm});
            skSolve(sketch);
        }
        {
            var Q0;
            Q0=sQuery(id+"F8.wireOp",EDGE,"E32");
            extrude(context, id + "F9", {"bodyType" : ExtendedToolBodyType.SURFACE, "surfaceEntities" : qUnion([Q0]), "oppositeDirection" : true, "depth" : 67.82 * mm});
        }
        {
            var Q0;
            {var subQ0=sQuery(id+"F0.wireOp",EDGE,"E1");Q0=makeQuery(id+"F7.imprint","IMPRINT",FACE,{"disambiguationData":[TD([[makeQuery(id+"F7.imprint","IMPRINT",EDGE,{"derivedFrom":makeQuery(id+"F1.opRevolve","SWEPT_EDGE",EDGE,{"disambiguationData":[OSD([subQ0,sQuery(id+"F0.wireOp",EDGE,"E12.filletArc")])]})}),1.0]])]});}
            extrude(context, id + "F10", {"entities" : qUnion([Q0]), "operationType" : NewBodyOperationType.ADD, "flatOperationType" : FlatOperationType.REMOVE, "oppositeDirection" : true, "offsetDistance" : 25.4 * mm, "depth" : 25.4 * mm, "domain" : OperationDomain.MODEL});
        }
    });
